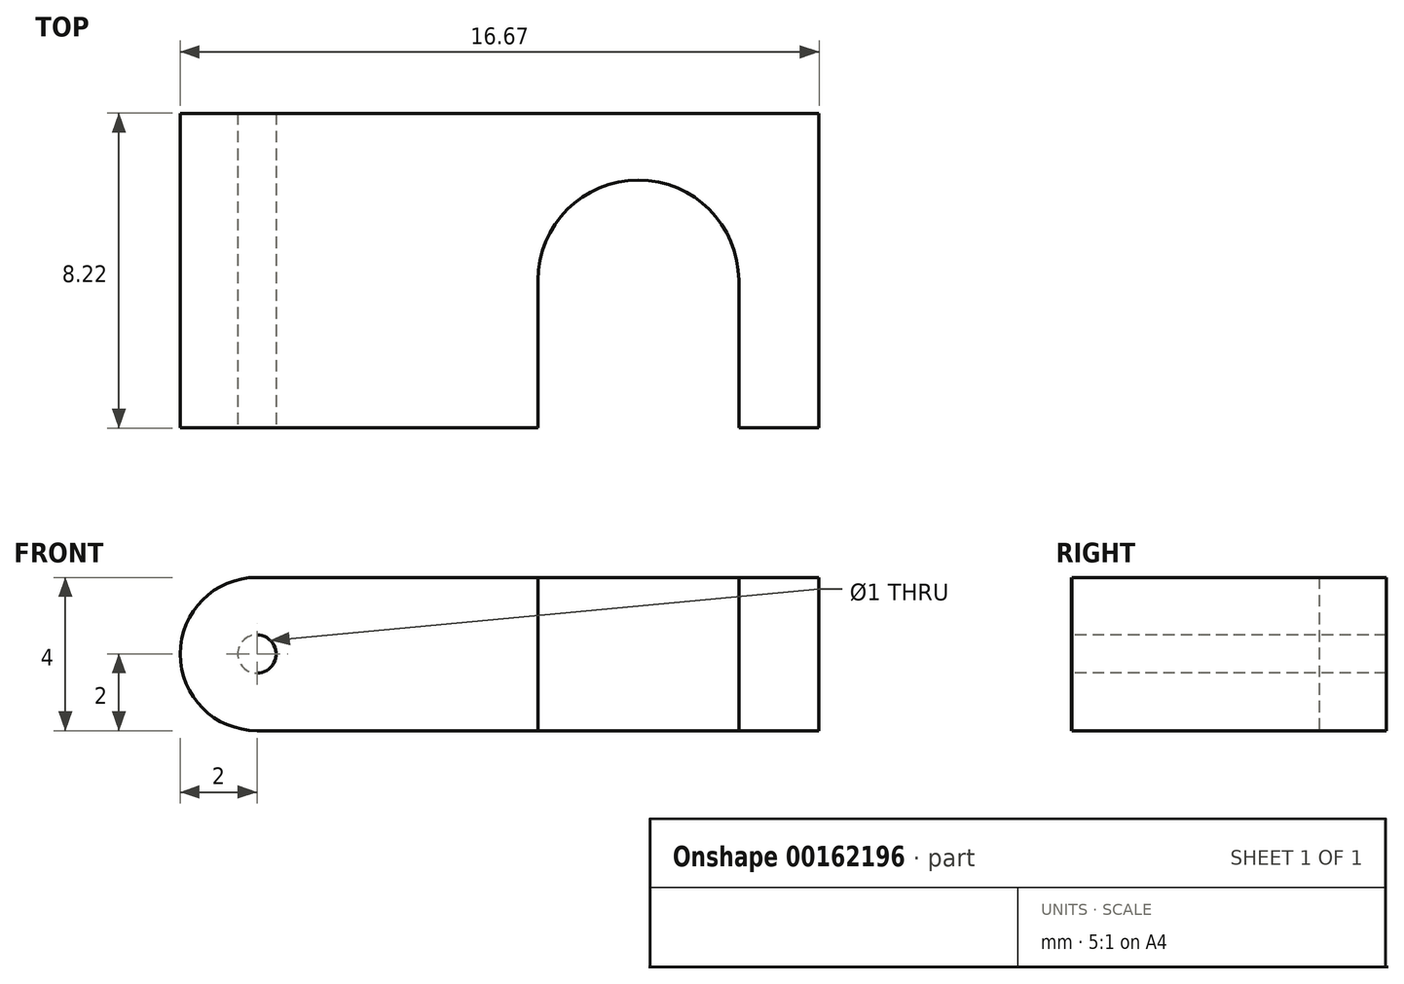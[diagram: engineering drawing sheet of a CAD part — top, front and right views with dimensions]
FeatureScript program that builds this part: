
annotation { "Feature Type Name" : "Feature", "Feature Type Description" : "" }
export const myFeature = defineFeature(function(context is Context, id is Id, definition is map)
    precondition{}
    {
        {
            var Q0;
            Q0=qCreatedBy(makeId("Top.planeOp"),FACE);
            var sketch = newSketch(context, id + "F0", { "sketchPlane" : qUnion([Q0])});
            skLineSegment(sketch, "E0.bottom", {"start": v(0, 0) * mm, "end": v(14.67, 0) * mm});
            skLineSegment(sketch, "E0.top", {"start": v(0, 8.2) * mm, "end": v(14.67, 8.2) * mm});
            skLineSegment(sketch, "E0.left", {"start": v(0, 0) * mm, "end": v(0, 8.2) * mm});
            skLineSegment(sketch, "E0.right", {"start": v(14.67, 0) * mm, "end": v(14.67, 8.2) * mm});
            skLineSegment(sketch, "E1", {"start": v(12.57, 0) * mm, "end": v(12.57, 3.84) * mm});
            skLineSegment(sketch, "E2", {"start": v(7.33, 0) * mm, "end": v(7.33, 3.84) * mm});
            skArc(sketch, "E3", {"start": v(12.57, 3.84) * mm, "mid": v(9.95, 6.46) * mm, "end": v(7.33, 3.84) * mm});
            skSolve(sketch);
        }
        {
            var Q0;
            Q0=makeQuery(id+"F0.imprint","IMPRINT",FACE,{"disambiguationData":[TD([[makeQuery(id+"F0.imprint","IMPRINT",EDGE,{"derivedFrom":sQuery(id+"F0.wireOp",EDGE,"E0.top")}),-1.0]])]});
            extrude(context, id + "F1", {"entities" : qUnion([Q0]), "depth" : 4 * mm});
        }
        {
            var Q0;
            Q0=makeQuery(id+"F1.opExtrude","SWEPT_FACE",FACE,{"disambiguationData":[OSD([sQuery(id+"F0.wireOp",EDGE,"E0.top")])]});
            var sketch = newSketch(context, id + "F2", { "sketchPlane" : qUnion([Q0])});
            skArc(sketch, "E4", {"start": v(0, 0) * mm, "mid": v(2, 2) * mm, "end": v(0, 4) * mm});
            skSolve(sketch);
        }
        {
            var Q0;
            Q0=makeQuery(id+"F2.imprint","IMPRINT",FACE,{"disambiguationData":[TD([[makeQuery(id+"F2.imprint","IMPRINT",EDGE,{"derivedFrom":sQuery(id+"F2.wireOp",EDGE,"E4")}),1.0]])]});
            extrude(context, id + "F3", {"entities" : qUnion([Q0]), "operationType" : NewBodyOperationType.ADD, "oppositeDirection" : true, "depth" : 8.21 * mm});
        }
        {
            var Q0;
            Q0=qCreatedBy(makeId("Front.planeOp"),FACE);
            var sketch = newSketch(context, id + "F4", { "sketchPlane" : qUnion([Q0])});
            skCircle(sketch, "E5", {"center": v(0, 2) * mm, "radius": 0.5 * mm});
            skSolve(sketch);
        }
        {
            var Q0;
            Q0=makeQuery(id+"F4.imprint","IMPRINT",FACE,{"disambiguationData":[TD([[makeQuery(id+"F4.imprint","IMPRINT",EDGE,{"derivedFrom":sQuery(id+"F4.wireOp",EDGE,"E5")}),1.0]])]});
            extrude(context, id + "F5", {"entities" : qUnion([Q0]), "operationType" : NewBodyOperationType.REMOVE, "oppositeDirection" : true, "depth" : 25 * mm});
        }
    });
